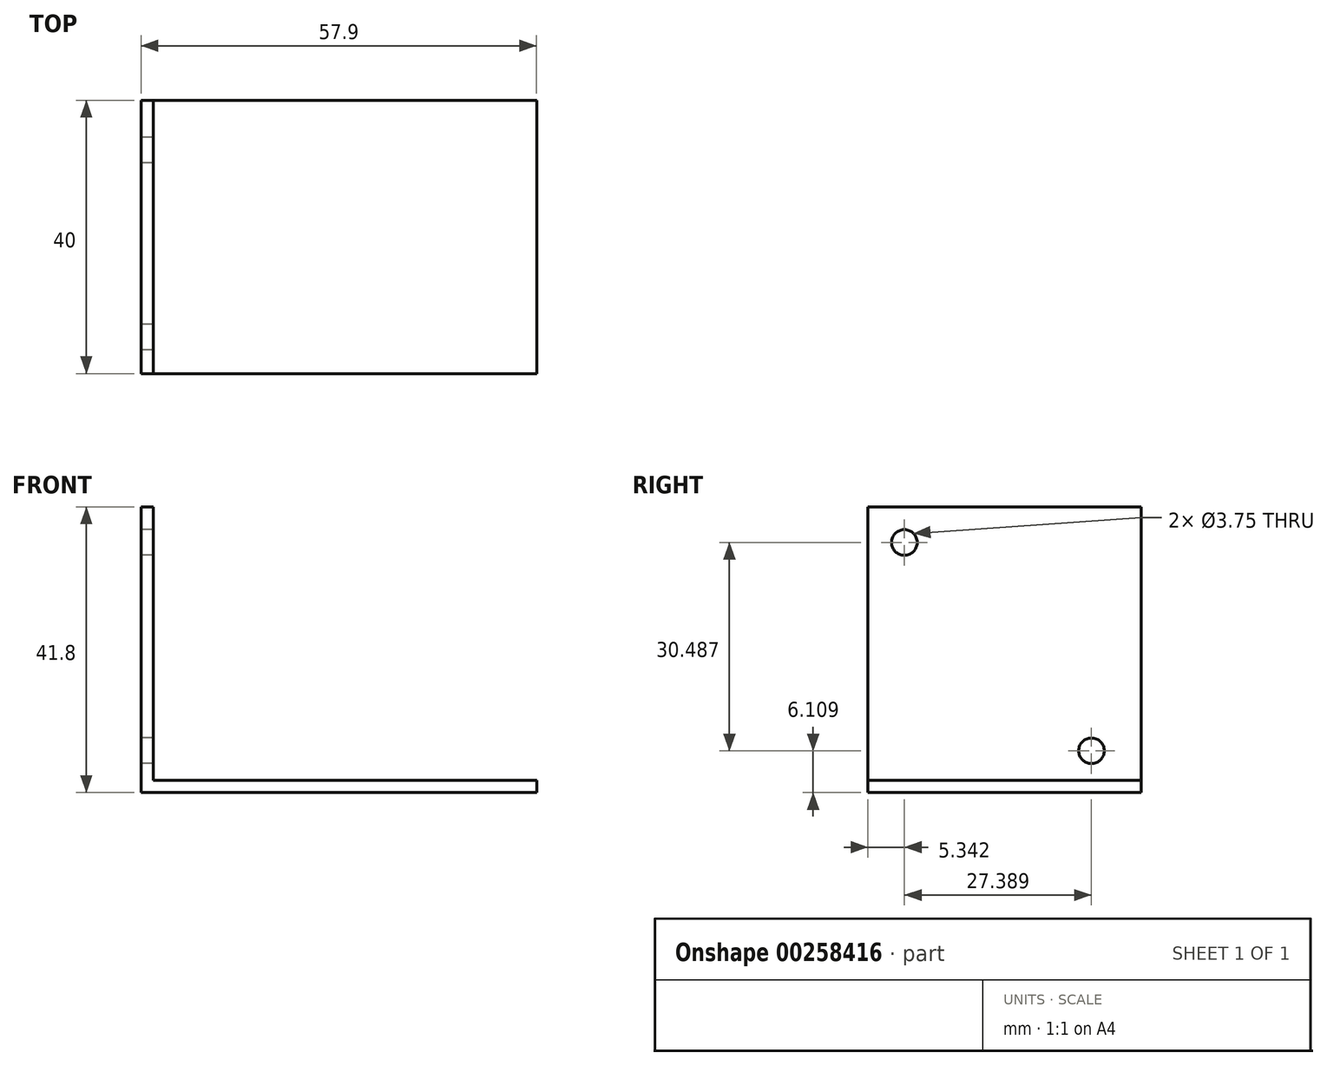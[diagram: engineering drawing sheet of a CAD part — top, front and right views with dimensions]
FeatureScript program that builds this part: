
annotation { "Feature Type Name" : "Feature", "Feature Type Description" : "" }
export const myFeature = defineFeature(function(context is Context, id is Id, definition is map)
    precondition{}
    {
        {
            var Q0;
            Q0=qCreatedBy(makeId("Top.planeOp"),FACE);
            var sketch = newSketch(context, id + "F0", { "sketchPlane" : qUnion([Q0])});
            skLineSegment(sketch, "E0.bottom", {"start": v(28.95, -20) * mm, "end": v(-28.95, -20) * mm});
            skLineSegment(sketch, "E0.top", {"start": v(28.95, 20) * mm, "end": v(-28.95, 20) * mm});
            skLineSegment(sketch, "E0.left", {"start": v(28.95, -20) * mm, "end": v(28.95, 20) * mm});
            skLineSegment(sketch, "E0.right", {"start": v(-28.95, -20) * mm, "end": v(-28.95, 20) * mm});
            skPoint(sketch, "E0.middle", {"position": v(0, 0) * mm});
            skSolve(sketch);
        }
        {
            var Q0;
            Q0=makeQuery(id+"F0.imprint","IMPRINT",FACE,{"disambiguationData":[TD([[makeQuery(id+"F0.imprint","IMPRINT",EDGE,{"derivedFrom":sQuery(id+"F0.wireOp",EDGE,"E0.bottom")}),-1.0]])]});
            extrude(context, id + "F1", {"entities" : qUnion([Q0]), "depth" : 1.8 * mm});
        }
        {
            var Q0;
            Q0=makeQuery(id+"F1.opExtrude","CAP_FACE",FACE,{"disambiguationData":[OSD([sQuery(id+"F0.wireOp",EDGE,"E0.bottom"),sQuery(id+"F0.wireOp",EDGE,"E0.top"),sQuery(id+"F0.wireOp",EDGE,"E0.left"),sQuery(id+"F0.wireOp",EDGE,"E0.right")])],"isStart":false});
            var sketch = newSketch(context, id + "F2", { "sketchPlane" : qUnion([Q0])});
            skLineSegment(sketch, "E1.bottom", {"start": v(-28.95, -20) * mm, "end": v(-27.15, -20) * mm});
            skLineSegment(sketch, "E1.top", {"start": v(-28.95, 20) * mm, "end": v(-27.15, 20) * mm});
            skLineSegment(sketch, "E1.left", {"start": v(-28.95, -20) * mm, "end": v(-28.95, 20) * mm});
            skLineSegment(sketch, "E1.right", {"start": v(-27.15, -20) * mm, "end": v(-27.15, 20) * mm});
            skPoint(sketch, "E1.middle", {"position": v(-28.05, 0) * mm});
            skSolve(sketch);
        }
        {
            var Q0;
            Q0=makeQuery(id+"F2.imprint","IMPRINT",FACE,{"disambiguationData":[TD([[makeQuery(id+"F2.imprint","IMPRINT",EDGE,{"derivedFrom":sQuery(id+"F2.wireOp",EDGE,"E1.bottom")}),-1.0]])]});
            extrude(context, id + "F3", {"entities" : qUnion([Q0]), "operationType" : NewBodyOperationType.ADD, "depth" : 40 * mm});
        }
        {
            var Q0;
            Q0=makeQuery(id+"F3.boolean.opBoolean","MERGE",FACE,{"derivedFrom":[makeQuery(id+"F1.opExtrude","SWEPT_FACE",FACE,{"disambiguationData":[OSD([sQuery(id+"F0.wireOp",EDGE,"E0.right")])]}),makeQuery(id+"F3.opExtrude","SWEPT_FACE",FACE,{"disambiguationData":[OSD([sQuery(id+"F2.wireOp",EDGE,"E1.left")])]})]});
            var sketch = newSketch(context, id + "F4", { "sketchPlane" : qUnion([Q0])});
            skCircle(sketch, "E2", {"center": v(14.66, 36.6) * mm, "radius": 1.88 * mm});
            skCircle(sketch, "E3", {"center": v(-12.73, 6.1) * mm, "radius": 1.88 * mm});
            skSolve(sketch);
        }
        {
            var Q0;
            Q0 = qSketchRegion(id + "F4", true);
            extrude(context, id + "F5", {"entities" : qUnion([Q0]), "operationType" : NewBodyOperationType.REMOVE, "oppositeDirection" : true, "depth" : 9.2 * mm});
        }
    });
